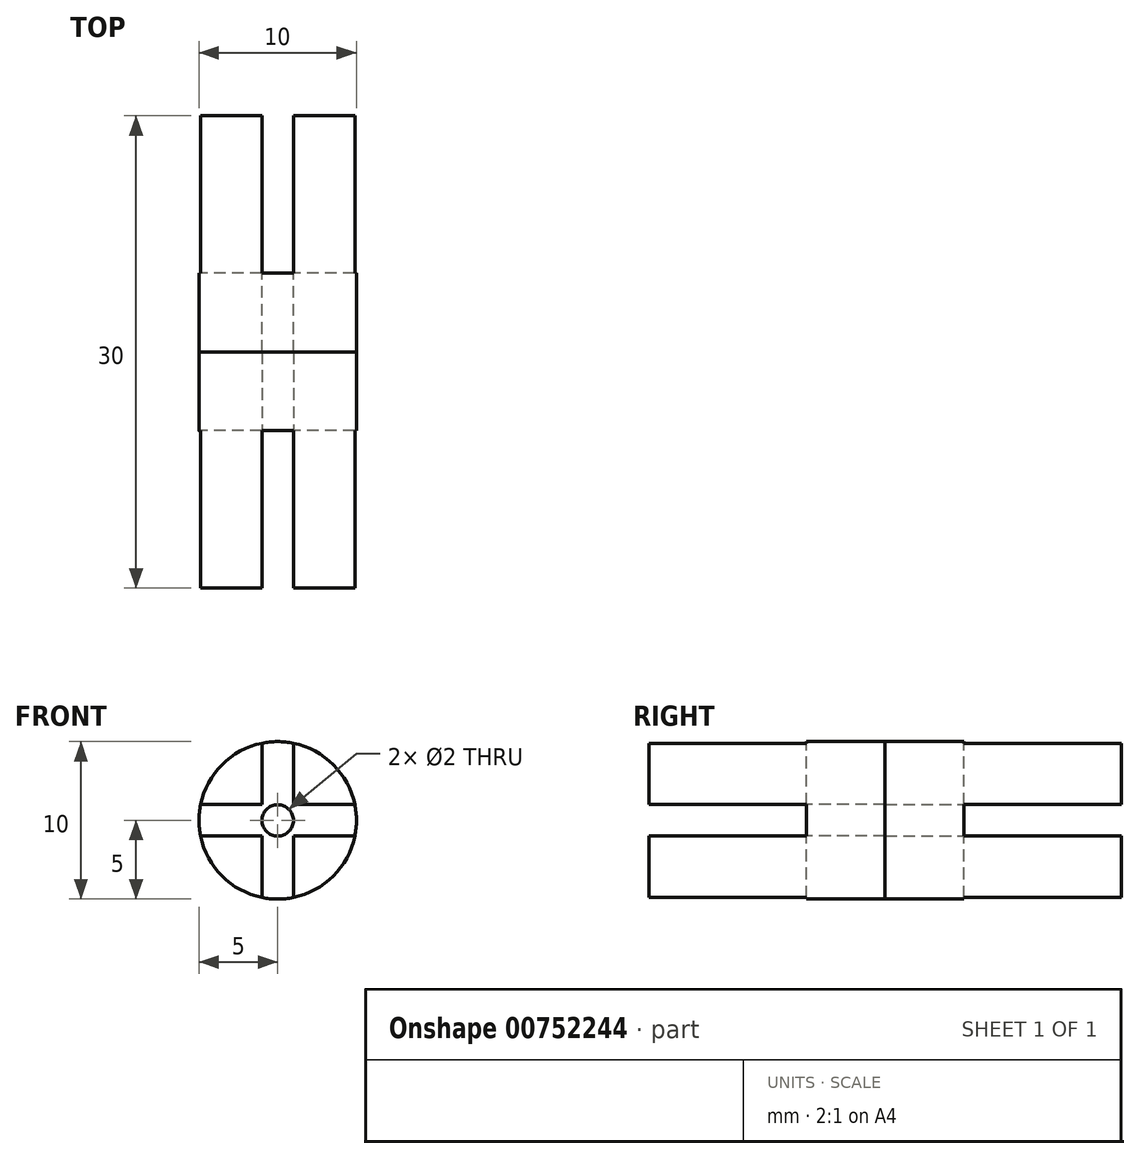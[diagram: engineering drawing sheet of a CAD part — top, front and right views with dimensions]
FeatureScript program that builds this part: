
annotation { "Feature Type Name" : "Feature", "Feature Type Description" : "" }
export const myFeature = defineFeature(function(context is Context, id is Id, definition is map)
    precondition{}
    {
        {
            var Q0;
            Q0=qCreatedBy(makeId("Front.planeOp"),FACE);
            var sketch = newSketch(context, id + "F0", { "sketchPlane" : qUnion([Q0])});
            skCircle(sketch, "E0", {"center": v(0, 0) * mm, "radius": 5 * mm});
            skSolve(sketch);
        }
        {
            var Q0;
            Q0 = qSketchRegion(id + "F0", true);
            extrude(context, id + "F1", {"entities" : qUnion([Q0]), "depth" : 15 * mm, "offsetDistance" : 25 * mm});
        }
        {
            var Q0;
            Q0=makeQuery(id+"F1.opExtrude","CAP_FACE",FACE,{"disambiguationData":[OSD([sQuery(id+"F0.wireOp",EDGE,"E0")])],"isStart":false});
            var sketch = newSketch(context, id + "F2", { "sketchPlane" : qUnion([Q0])});
            skLineSegment(sketch, "E1.left", {"start": v(1, -4.9) * mm, "end": v(1, -1) * mm});
            skLineSegment(sketch, "E1.right", {"start": v(-1, -4.9) * mm, "end": v(-1, -1) * mm});
            skPoint(sketch, "E1.middle", {"position": v(0, 0) * mm});
            skLineSegment(sketch, "E2.bottom", {"start": v(4.9, -1) * mm, "end": v(1, -1) * mm});
            skLineSegment(sketch, "E2.top", {"start": v(4.9, 1) * mm, "end": v(1, 1) * mm});
            skLineSegment(sketch, "E3.trimOffspring", {"start": v(-1, 1) * mm, "end": v(-1, 4.9) * mm});
            skLineSegment(sketch, "E4.trimOffspring", {"start": v(-1, 1) * mm, "end": v(-4.9, 1) * mm});
            skLineSegment(sketch, "E5.trimOffspring", {"start": v(1, 1) * mm, "end": v(1, 4.9) * mm});
            skLineSegment(sketch, "E6.trimOffspring", {"start": v(-1, -1) * mm, "end": v(-4.9, -1) * mm});
            skSolve(sketch);
        }
        {
            var Q0;
            {var subQ0=sQuery(id+"F2.wireOp",EDGE,"E1.left");Q0=makeQuery(id+"F2.imprint","IMPRINT",FACE,{"disambiguationData":[TD([[makeQuery(id+"F2.imprint","IMPRINT",EDGE,{"derivedFrom":subQ0}),1.0]])]});}
            extrude(context, id + "F3", {"entities" : qUnion([Q0]), "operationType" : NewBodyOperationType.REMOVE, "oppositeDirection" : true, "depth" : 10 * mm, "offsetDistance" : 25 * mm});
        }
        {
            var Q0;
            Q0=makeQuery(id+"F3.boolean.opBoolean","COPY",FACE,{"derivedFrom":makeQuery(id+"F3.opExtrude","CAP_FACE",FACE,{"disambiguationData":[OSD([sQuery(id+"F0.wireOp",EDGE,"E0"),sQuery(id+"F2.wireOp",EDGE,"E1.left"),sQuery(id+"F2.wireOp",EDGE,"E1.right"),sQuery(id+"F2.wireOp",EDGE,"E2.bottom"),sQuery(id+"F2.wireOp",EDGE,"E2.top"),sQuery(id+"F2.wireOp",EDGE,"E3.trimOffspring"),sQuery(id+"F2.wireOp",EDGE,"E4.trimOffspring"),sQuery(id+"F2.wireOp",EDGE,"E5.trimOffspring"),sQuery(id+"F2.wireOp",EDGE,"E6.trimOffspring")])],"isStart":false})});
            var sketch = newSketch(context, id + "F4", { "sketchPlane" : qUnion([Q0])});
            skCircle(sketch, "E7", {"center": v(0, 0) * mm, "radius": 1 * mm});
            skSolve(sketch);
        }
        {
            var Q0;
            Q0 = qSketchRegion(id + "F4", true);
            extrude(context, id + "F5", {"entities" : qUnion([Q0]), "operationType" : NewBodyOperationType.REMOVE, "endBound" : BoundingType.THROUGH_ALL, "oppositeDirection" : true, "depth" : 25 * mm, "offsetDistance" : 25 * mm});
        }
        {
            var Q0;
            Q0=makeQuery(id+"F1.opExtrude","SWEPT_BODY",BODY,{"disambiguationData":[OSD([sQuery(id+"F0.wireOp",EDGE,"E0")])]});
            var Q1;
            Q1=qCreatedBy(makeId("Front.planeOp"),FACE);
            mirror(context, id + "F6", {"entities" : qUnion([Q0]), "mirrorPlane" : qUnion([Q1])});
        }
    });
